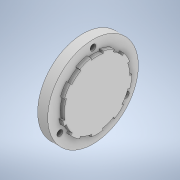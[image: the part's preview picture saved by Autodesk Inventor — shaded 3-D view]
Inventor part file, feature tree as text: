
AUTODESK INVENTOR PART (.ipt)
format: ipt  version: 2021 (Build 250183000, 183)  size: 180,736 bytes
history: native  units: mm
features: other x3, extrude x2, sketch x2, projected_geometry x1
ambient origin geometry x8: Origin, YZ Plane, XZ Plane, XY Plane, X Axis, Y Axis, Z Axis, Center Point
bodies: Solid1 (feature_tree)
feature tree (8):
  other  "wheel_gearing_mount_short.ipt"
  extrude  "Extrusion3"  Depth=10.0mm TaperAngle=0.0deg
  extrude  "Extrusion4"  [1 undecoded]
  other  "Solid1::wheel_gearing_mount_short.ipt"
  other  "TaggingFeature2"
  sketch  "Sketch4"  dims[d5=10.0mm d6=10.0mm d7=0.0mm]
  projected_geometry  "Projected Loop3"
  sketch  "Sketch5"  dims[d8=10.0mm d9=0.0mm]
note: 1 required parameter value undecoded (feature->parameter linkage not recoverable at this tier; creation-order binding heuristic only, values carry confidence <= 0.55)
